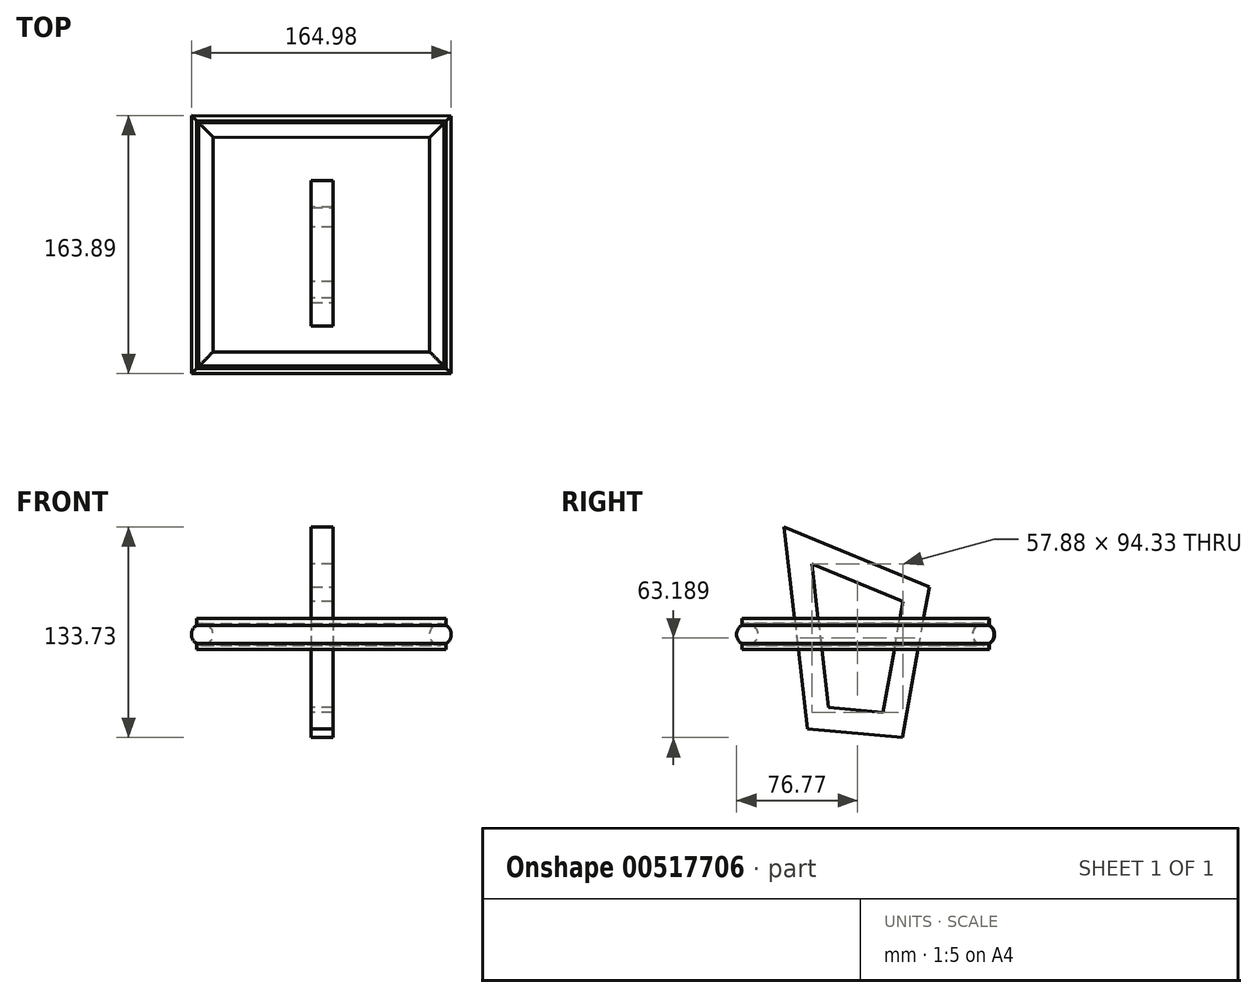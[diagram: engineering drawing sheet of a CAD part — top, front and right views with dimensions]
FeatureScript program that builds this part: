
annotation { "Feature Type Name" : "Feature", "Feature Type Description" : "" }
export const myFeature = defineFeature(function(context is Context, id is Id, definition is map)
    precondition{}
    {
        {
            var Q0;
            Q0=qCreatedBy(makeId("Top.planeOp"),FACE);
            var sketch = newSketch(context, id + "F0", { "sketchPlane" : qUnion([Q0])});
            skLineSegment(sketch, "E0", {"start": v(-76.92, 75.93) * mm, "end": v(-76.92, -74.65) * mm});
            skLineSegment(sketch, "E1", {"start": v(-76.92, -74.65) * mm, "end": v(74.76, -74.65) * mm});
            skLineSegment(sketch, "E2", {"start": v(74.76, -74.65) * mm, "end": v(74.76, 75.67) * mm});
            skLineSegment(sketch, "E3", {"start": v(74.76, 75.67) * mm, "end": v(-76.92, 75.93) * mm});
            skSolve(sketch);
        }
        {
            var Q0;
            Q0=qCreatedBy(makeId("Front.planeOp"),FACE);
            var sketch = newSketch(context, id + "F1", { "sketchPlane" : qUnion([Q0])});
            skCircle(sketch, "E4", {"center": v(-76.7, 0) * mm, "radius": 6.86 * mm});
            skLineSegment(sketch, "E5", {"start": v(-76.7, 0) * mm, "end": v(-80.28, 10.16) * mm});
            skLineSegment(sketch, "E6", {"start": v(-80.28, 10.16) * mm, "end": v(-80.28, -9.6) * mm});
            skLineSegment(sketch, "E7", {"start": v(-80.28, -9.6) * mm, "end": v(-76.7, 0) * mm});
            skSolve(sketch);
        }
        {
            var Q0;
            Q0 = qSketchRegion(id + "F1", true);
            var Q1;
            Q1 = qConstructionFilter(qBodyType(qCreatedBy(id + "F0" ,EDGE), BodyType.WIRE), ConstructionObject.NO);
            sweep(context, id + "F2", {"profiles" : qUnion([Q0]), "path" : qUnion([Q1])});
        }
        {
            var Q0;
            Q0=qCreatedBy(makeId("Right.planeOp"),FACE);
            var sketch = newSketch(context, id + "F3", { "sketchPlane" : qUnion([Q0])});
            skLineSegment(sketch, "E8", {"start": v(-43.49, 58.14) * mm, "end": v(-30.48, -54.14) * mm});
            skLineSegment(sketch, "E9", {"start": v(-30.48, -54.14) * mm, "end": v(18.68, -58.5) * mm});
            skLineSegment(sketch, "E10", {"start": v(18.68, -58.5) * mm, "end": v(33.9, 26.27) * mm});
            skLineSegment(sketch, "E11", {"start": v(33.9, 26.27) * mm, "end": v(-43.49, 58.14) * mm});
            skSolve(sketch);
        }
        {
            var Q0;
            Q0=qCreatedBy(makeId("Top.planeOp"),FACE);
            var sketch = newSketch(context, id + "F4", { "sketchPlane" : qUnion([Q0])});
            skLineSegment(sketch, "E12", {"start": v(0, 29.35) * mm, "end": v(-7.69, 29.35) * mm});
            skLineSegment(sketch, "E13", {"start": v(-7.69, 29.35) * mm, "end": v(-7.69, 20.63) * mm});
            skLineSegment(sketch, "E14", {"start": v(-7.69, 20.63) * mm, "end": v(6.49, 20.63) * mm});
            skLineSegment(sketch, "E15", {"start": v(6.49, 20.63) * mm, "end": v(6.49, 35.74) * mm});
            skLineSegment(sketch, "E16", {"start": v(6.49, 35.74) * mm, "end": v(-7.69, 35.74) * mm});
            skLineSegment(sketch, "E17", {"start": v(-7.69, 35.74) * mm, "end": v(-7.69, 29.35) * mm});
            skSolve(sketch);
        }
        {
            var Q0;
            Q0 = qSketchRegion(id + "F4", true);
            var Q1;
            Q1 = qConstructionFilter(qBodyType(qCreatedBy(id + "F3" ,EDGE), BodyType.WIRE), ConstructionObject.NO);
            sweep(context, id + "F5", {"profiles" : qUnion([Q0]), "path" : qUnion([Q1])});
        }
    });
